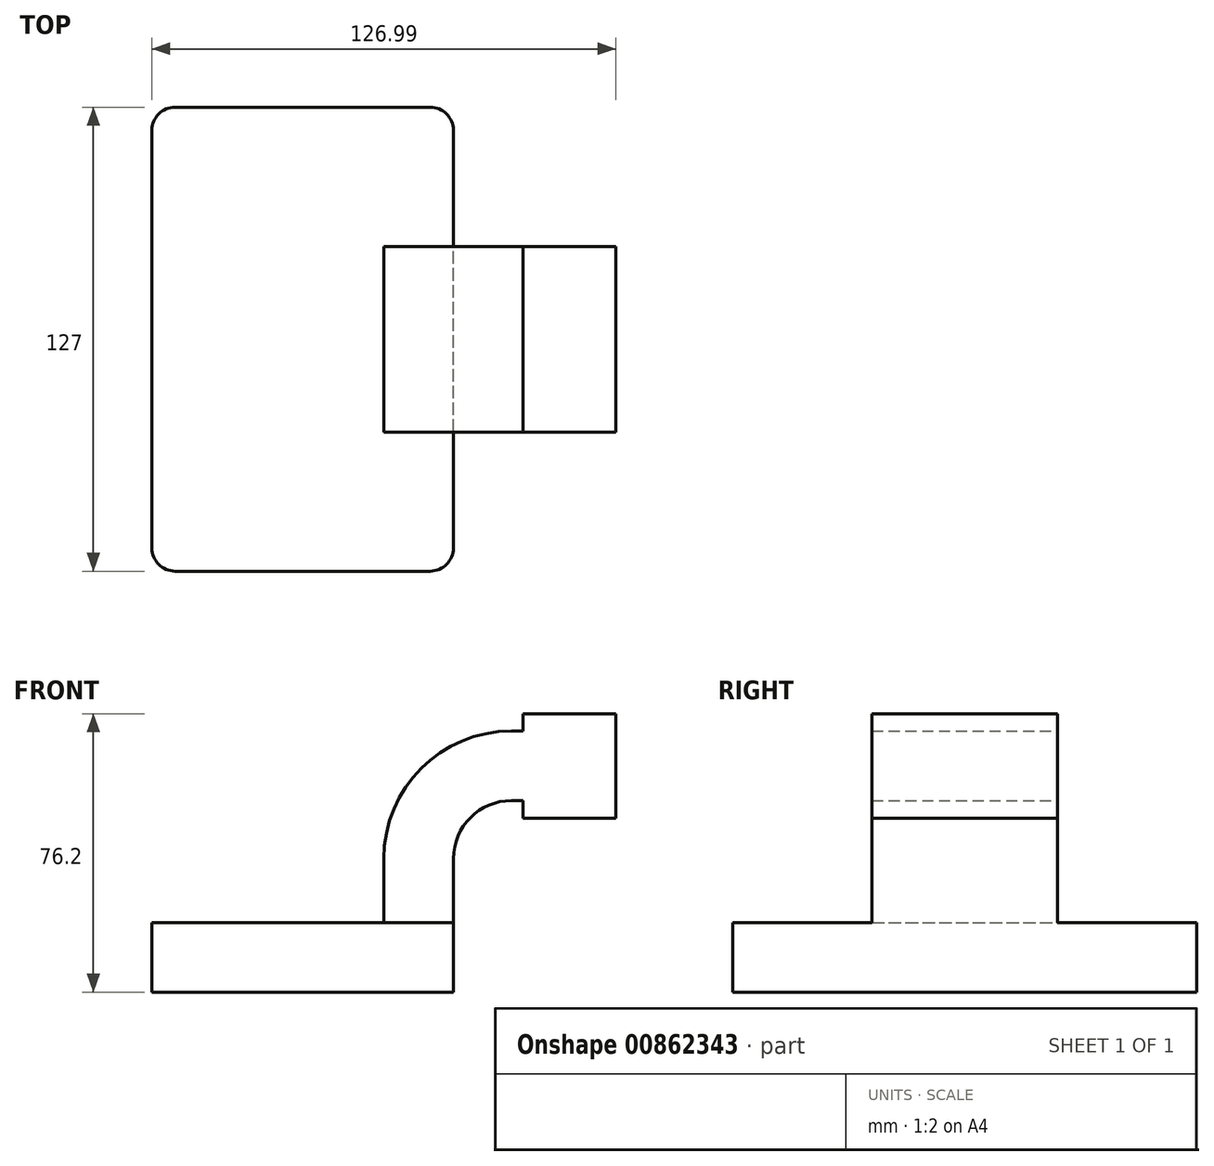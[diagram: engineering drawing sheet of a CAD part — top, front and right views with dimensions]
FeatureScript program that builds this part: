
annotation { "Feature Type Name" : "Feature", "Feature Type Description" : "" }
export const myFeature = defineFeature(function(context is Context, id is Id, definition is map)
    precondition{}
    {
        {
            var Q0;
            Q0=qCreatedBy(makeId("Front.planeOp"),FACE);
            var sketch = newSketch(context, id + "F0", { "sketchPlane" : qUnion([Q0])});
            skLineSegment(sketch, "E0.bottom", {"start": v(-41.28, -9.52) * mm, "end": v(41.28, -9.52) * mm});
            skLineSegment(sketch, "E0.top", {"start": v(-41.28, 9.52) * mm, "end": v(41.28, 9.52) * mm});
            skLineSegment(sketch, "E0.left", {"start": v(-41.28, -9.52) * mm, "end": v(-41.28, 9.52) * mm});
            skLineSegment(sketch, "E0.right", {"start": v(41.28, -9.53) * mm, "end": v(41.28, 9.52) * mm});
            skPoint(sketch, "E0.middle", {"position": v(0, 0) * mm});
            skLineSegment(sketch, "E1.bottom", {"start": v(111.13, 38.1) * mm, "end": v(60.32, 38.1) * mm});
            skLineSegment(sketch, "E1.top", {"start": v(111.13, 66.68) * mm, "end": v(60.33, 66.68) * mm});
            skLineSegment(sketch, "E1.left", {"start": v(111.13, 38.1) * mm, "end": v(111.13, 66.68) * mm});
            skLineSegment(sketch, "E1.right", {"start": v(60.33, 38.1) * mm, "end": v(60.33, 66.67) * mm});
            skPoint(sketch, "E1.middle", {"position": v(85.73, 52.39) * mm});
            skLineSegment(sketch, "E2", {"start": v(41.28, 9.52) * mm, "end": v(41.28, 27) * mm});
            skArc(sketch, "E3", {"start": v(41.27, 27) * mm, "mid": v(45.92, 38.23) * mm, "end": v(57.15, 42.88) * mm});
            skLineSegment(sketch, "E4", {"start": v(57.15, 42.88) * mm, "end": v(85.73, 42.88) * mm});
            skLineSegment(sketch, "E5.0", {"start": v(57.15, 61.93) * mm, "end": v(85.73, 61.93) * mm});
            skArc(sketch, "E5.1", {"start": v(22.23, 27) * mm, "mid": v(32.45, 51.7) * mm, "end": v(57.15, 61.93) * mm});
            skLineSegment(sketch, "E5.2", {"start": v(22.23, 9.52) * mm, "end": v(22.23, 27) * mm});
            skLineSegment(sketch, "E6", {"start": v(85.73, 42.88) * mm, "end": v(85.73, 61.93) * mm});
            skLineSegment(sketch, "E7", {"start": v(85.73, 61.93) * mm, "end": v(85.72, 66.68) * mm});
            skLineSegment(sketch, "E8", {"start": v(85.72, 42.88) * mm, "end": v(85.72, 38.1) * mm});
            skFitSpline(sketch, "E9", {"points": [v(-41.28, 9.53) * mm, v(57.15, 61.93) * mm], "startDerivative": vector(28.63, 105.87) * mm, "endDerivative": vector(113.34, -2.24) * mm});
            skSolve(sketch);
        }
        {
            var Q0;
            Q0=makeQuery(id+"F0.imprint","IMPRINT",FACE,{"disambiguationData":[TD([[makeQuery(id+"F0.imprint","IMPRINT",EDGE,{"derivedFrom":sQuery(id+"F0.wireOp",EDGE,"E0.bottom")}),1.0]])]});
            extrude(context, id + "F1", {"entities" : qUnion([Q0]), "endBound" : BoundingType.SYMMETRIC, "depth" : 127 * mm, "offsetDistance" : 25.4 * mm});
        }
        {
            var Q0;
            {var subQ1=sQuery(id+"F0.wireOp",EDGE,"E2");Q0=makeQuery(id+"F0.imprint","IMPRINT",FACE,{"disambiguationData":[TD([[makeQuery(id+"F0.imprint","IMPRINT",EDGE,{"derivedFrom":subQ1}),1.0]])]});}
            var Q1;
            {var subQ5=sQuery(id+"F0.wireOp",EDGE,"E6");Q1=makeQuery(id+"F0.imprint","IMPRINT",FACE,{"disambiguationData":[TD([[makeQuery(id+"F0.imprint","IMPRINT",EDGE,{"derivedFrom":subQ5}),1.0]])]});}
            var Q2;
            {var subQ3=sQuery(id+"F0.wireOp",EDGE,"E7");Q2=makeQuery(id+"F0.imprint","IMPRINT",FACE,{"disambiguationData":[TD([[makeQuery(id+"F0.imprint","IMPRINT",EDGE,{"derivedFrom":subQ3}),1.0]])]});}
            var Q3;
            {var subQ3=sQuery(id+"F0.wireOp",EDGE,"E8");Q3=makeQuery(id+"F0.imprint","IMPRINT",FACE,{"disambiguationData":[TD([[makeQuery(id+"F0.imprint","IMPRINT",EDGE,{"derivedFrom":subQ3}),-1.0]])]});}
            extrude(context, id + "F2", {"entities" : qUnion([Q0, Q1, Q2, Q3]), "operationType" : NewBodyOperationType.ADD, "endBound" : BoundingType.SYMMETRIC, "depth" : 50.8 * mm, "offsetDistance" : 25.4 * mm});
        }
        {
            var Q0;
            Q0=makeQuery(id+"F0.imprint","IMPRINT",FACE,{"disambiguationData":[TD([[makeQuery(id+"F0.imprint","IMPRINT",EDGE,{"derivedFrom":sQuery(id+"F0.wireOp",EDGE,"E5.1")}),1.0]])]});
            extrude(context, id + "F3", {"entities" : qUnion([Q0]), "operationType" : NewBodyOperationType.ADD, "endBound" : BoundingType.SYMMETRIC, "depth" : 15.88 * mm, "offsetDistance" : 25.4 * mm});
        }
        {
            var Q0;
            Q0=makeQuery(id+"F1.opExtrude","CAP_EDGE",EDGE,{"disambiguationData":[OSD([sQuery(id+"F0.wireOp",EDGE,"E0.left")])],"isStart":false});
            var Q1;
            Q1=makeQuery(id+"F1.opExtrude","CAP_EDGE",EDGE,{"disambiguationData":[OSD([sQuery(id+"F0.wireOp",EDGE,"E0.right")])],"isStart":false});
            var Q2;
            Q2=makeQuery(id+"F1.opExtrude","CAP_EDGE",EDGE,{"disambiguationData":[OSD([sQuery(id+"F0.wireOp",EDGE,"E0.right")])],"isStart":true});
            var Q3;
            Q3=makeQuery(id+"F1.opExtrude","CAP_EDGE",EDGE,{"disambiguationData":[OSD([sQuery(id+"F0.wireOp",EDGE,"E0.left")])],"isStart":true});
            fillet(context, id + "F4", {"entities" : qUnion([Q0, Q1, Q2, Q3]), "radius" : 6.35 * mm, "tangentPropagation" : true, "allowEdgeOverflow" : false});
        }
    });
